# Revit family: Table-Teknion-CWTM_C-D_Rectangular_Table_Flat_Wood-Metal_Edge_USB-R2020
name_source: partatom
category: Furniture
units: mm (PartAtom-declared; Revit-internal decimal feet)

## family parameters
Always vertical = Yes
Cut with Voids When Loaded = No
OmniClass Number = 23.40.20.00
OmniClass Title = General Furniture and Specialties
Room Calculation Point = No
Shared = Yes
Work Plane-Based = No

## types (3) — shared parameters
Assembly Code = E2020200
For Additional Finishes, please visit = https://assets.teknion.com
Infill Finish = Veneer - Teknion - VM - Sisal
Leg Exterior Finish = Veneer - Teknion - VM - Sisal
Leg Exterior Finish Note = Pick a Veneer below that matches the color of the Leg Metal Finish.
Leg Metal Finish = Paint - Teknion - Mica - Anthracite
Manufacturer = Teknion
Manufacturer Fax = 416.661.4586
Outer Glass = Glass - Teknion - CL - Clear
Part Number = CWTM
Product Documentation Link = https://assets.teknion.com
Product Line = C+D
Product Page URL = https://www.teknion.com
Series = Custom Wood
Sustainability Data = https://www.teknion.com
To render, please download texture images found here = https://assets.teknion.com
URL = www.teknion.com
Unit Weight URL = http://www.teknion.com
Warranty = http://www.teknion.com
White Solid Surface Top Finish = Wood - Teknion - MV - Solid Surface - Glacier White
Wood Edge Finish = Veneer - Teknion - VM - Sisal
Wood Edge Finish Note = Pick a Veneer below that matches the color of the Metal Leg.
zero-valued in all types: Default Elevation

## per-type parameters (varying)
| type | Backpainted Glass Top Finish | Depth | Description | Etched Backpainted Glass Top Finish | Model | Veneer Top Finish |
| Depth 54" | Back-painted Glass - K7 - Teknion - Very White | 54 " | Custom Wood C+D Rectangular Table, Flat Wood-Metal Edge USB, 54" Depth | Etched Back-painted Glass - HC - Teknion - Storm White | CWTM__54_ | Veneer -Teknion - UX - Rustic Oak - Brindle |
| Depth 48" | Back-painted Glass - J6 - Teknion - Gris | 48 " | Custom Wood C+D Rectangular Table, Flat Wood-Metal Edge USB, 48" Depth | Etched Back-painted Glass - HB - Teknion - Very White | CWTM__48_ | Veneer - Teknion - VM - Sisal |
| Depth 60" | Back-painted Glass - K1 - Teknion - Storm White | 60 " | Custom Wood C+D Rectangular Table, Flat Wood-Metal Edge USB, 60" Depth | Etched Back-painted Glass - HD - Teknion - Gris | CWTM__60_ | Veneer - Teknion - VF - Desert Fawn |

## geometry (parser evidence)
native form markers: Sweep x10
no freeform markers — native parametric forms only
